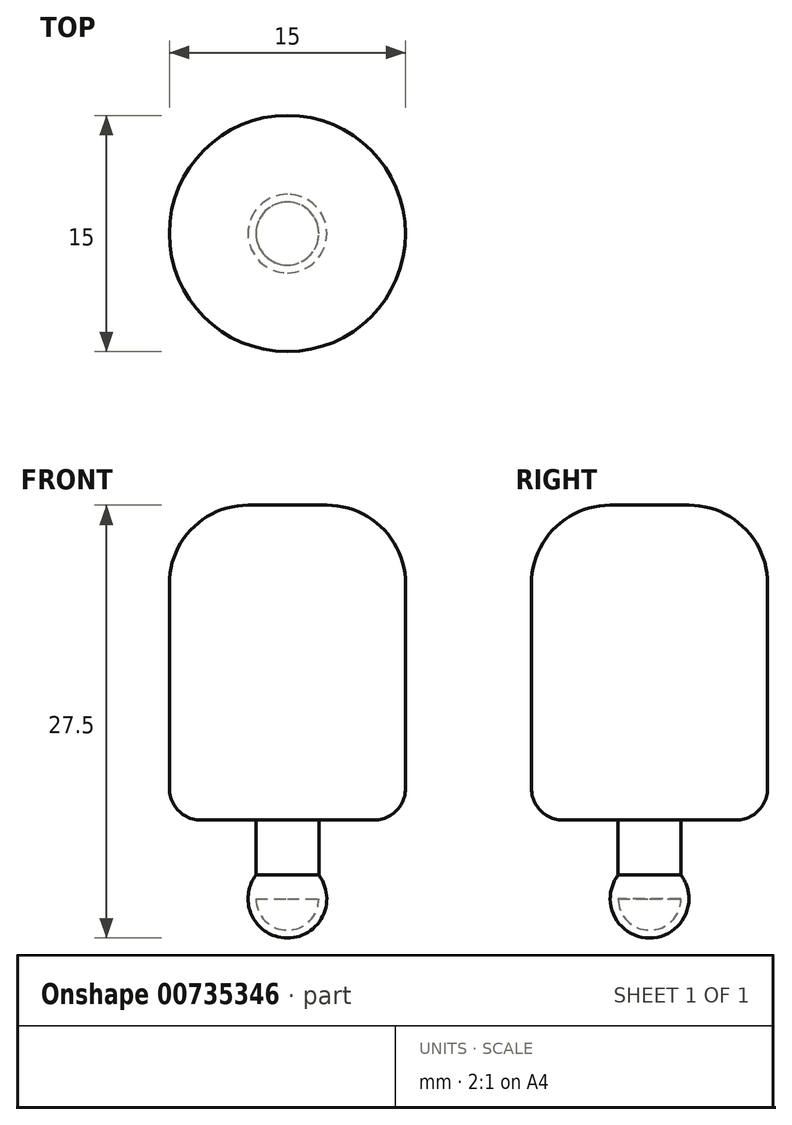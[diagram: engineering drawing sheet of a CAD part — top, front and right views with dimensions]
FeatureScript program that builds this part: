
annotation { "Feature Type Name" : "Feature", "Feature Type Description" : "" }
export const myFeature = defineFeature(function(context is Context, id is Id, definition is map)
    precondition{}
    {
        {
            var Q0;
            Q0=qCreatedBy(makeId("Top.planeOp"),FACE);
            var sketch = newSketch(context, id + "F0", { "sketchPlane" : qUnion([Q0])});
            skCircle(sketch, "E0", {"center": v(0, 0) * mm, "radius": 7.5 * mm});
            skSolve(sketch);
        }
        {
            var Q0;
            Q0 = qSketchRegion(id + "F0", true);
            extrude(context, id + "F1", {"entities" : qUnion([Q0]), "depth" : 20 * mm, "offsetDistance" : 25 * mm});
        }
        {
            var Q0;
            Q0=makeQuery(id+"F1.opExtrude","CAP_EDGE",EDGE,{"disambiguationData":[OSD([sQuery(id+"F0.wireOp",EDGE,"E0")])],"isStart":false});
            fillet(context, id + "F2", {"entities" : qUnion([Q0]), "radius" : 5 * mm, "tangentPropagation" : true, "allowEdgeOverflow" : false});
        }
        {
            var Q0;
            Q0=makeQuery(id+"F1.opExtrude","CAP_FACE",FACE,{"disambiguationData":[OSD([sQuery(id+"F0.wireOp",EDGE,"E0")])],"isStart":true});
            var sketch = newSketch(context, id + "F3", { "sketchPlane" : qUnion([Q0])});
            skCircle(sketch, "E1", {"center": v(0, 0) * mm, "radius": 2 * mm});
            skSolve(sketch);
        }
        {
            var Q0;
            Q0 = qSketchRegion(id + "F3", true);
            extrude(context, id + "F4", {"entities" : qUnion([Q0]), "operationType" : NewBodyOperationType.ADD, "depth" : 5 * mm, "offsetDistance" : 25 * mm});
        }
        {
            var Q0;
            Q0=makeQuery(id+"F4.opExtrude","CAP_FACE",FACE,{"disambiguationData":[OSD([sQuery(id+"F3.wireOp",EDGE,"E1")])],"isStart":false});
            var sketch = newSketch(context, id + "F5", { "sketchPlane" : qUnion([Q0])});
            skCircle(sketch, "E2", {"center": v(0, 0) * mm, "radius": 2.5 * mm});
            skLineSegment(sketch, "E3", {"start": v(0, 2.5) * mm, "end": v(0, -2.5) * mm});
            skSolve(sketch);
        }
        {
            var Q0;
            {var subQ0=sQuery(id+"F5.wireOp",EDGE,"E3");var subQ1=sQuery(id+"F5.wireOp",EDGE,"E2");var subQ2=makeQuery(id+"F5.imprint","INTERSECT",VERTEX,{"disambiguationData":[OD(0.0)],"derivedFrom":[subQ1,subQ0]});Q0=makeQuery(id+"F5.imprint","IMPRINT",FACE,{"disambiguationData":[TD([[makeQuery(id+"F5.imprint","IMPRINT",EDGE,{"disambiguationData":[TD([[subQ2,-1.0]])],"derivedFrom":subQ1}),1.0]])]});}
            var Q1;
            {var subQ0=sQuery(id+"F5.wireOp",EDGE,"E3");var subQ1=makeQuery(id+"F4.opExtrude","CAP_EDGE",EDGE,{"disambiguationData":[OSD([sQuery(id+"F3.wireOp",EDGE,"E1")])],"isStart":false});var subQ2=makeQuery(id+"F5.imprint","INTERSECT",VERTEX,{"disambiguationData":[OD(0.0)],"derivedFrom":[subQ1,subQ0]});Q1=makeQuery(id+"F5.imprint","IMPRINT",FACE,{"disambiguationData":[TD([[makeQuery(id+"F5.imprint","IMPRINT",EDGE,{"disambiguationData":[TD([[subQ2,-1.0]])],"derivedFrom":subQ0}),-1.0]])]});}
            var Q2;
            {var subQ0=sQuery(id+"F5.wireOp",EDGE,"E3");var subQ1=makeQuery(id+"F4.opExtrude","CAP_EDGE",EDGE,{"disambiguationData":[OSD([sQuery(id+"F3.wireOp",EDGE,"E1")])],"isStart":false});var subQ2=makeQuery(id+"F5.imprint","INTERSECT",VERTEX,{"disambiguationData":[OD(0.0)],"derivedFrom":[subQ1,subQ0]});Q2=makeQuery(id+"F5.imprint","IMPRINT",FACE,{"disambiguationData":[TD([[makeQuery(id+"F5.imprint","IMPRINT",EDGE,{"disambiguationData":[TD([[subQ2,-1.0]])],"derivedFrom":subQ0}),1.0]])]});}
            var Q3;
            Q3=sQuery(id+"F5.wireOp",EDGE,"E3");
            revolve(context, id + "F6", {"operationType" : NewBodyOperationType.ADD, "surfaceOperationType" : NewSurfaceOperationType.NEW, "entities" : qUnion([Q0, Q1, Q2]), "axis" : qUnion([Q3]), "revolveType" : RevolveType.FULL});
        }
        {
            var Q0;
            Q0=makeQuery(id+"F1.opExtrude","CAP_EDGE",EDGE,{"disambiguationData":[OSD([sQuery(id+"F0.wireOp",EDGE,"E0")])],"isStart":true});
            fillet(context, id + "F7", {"entities" : qUnion([Q0]), "radius" : 2 * mm, "tangentPropagation" : true, "allowEdgeOverflow" : false});
        }
    });
